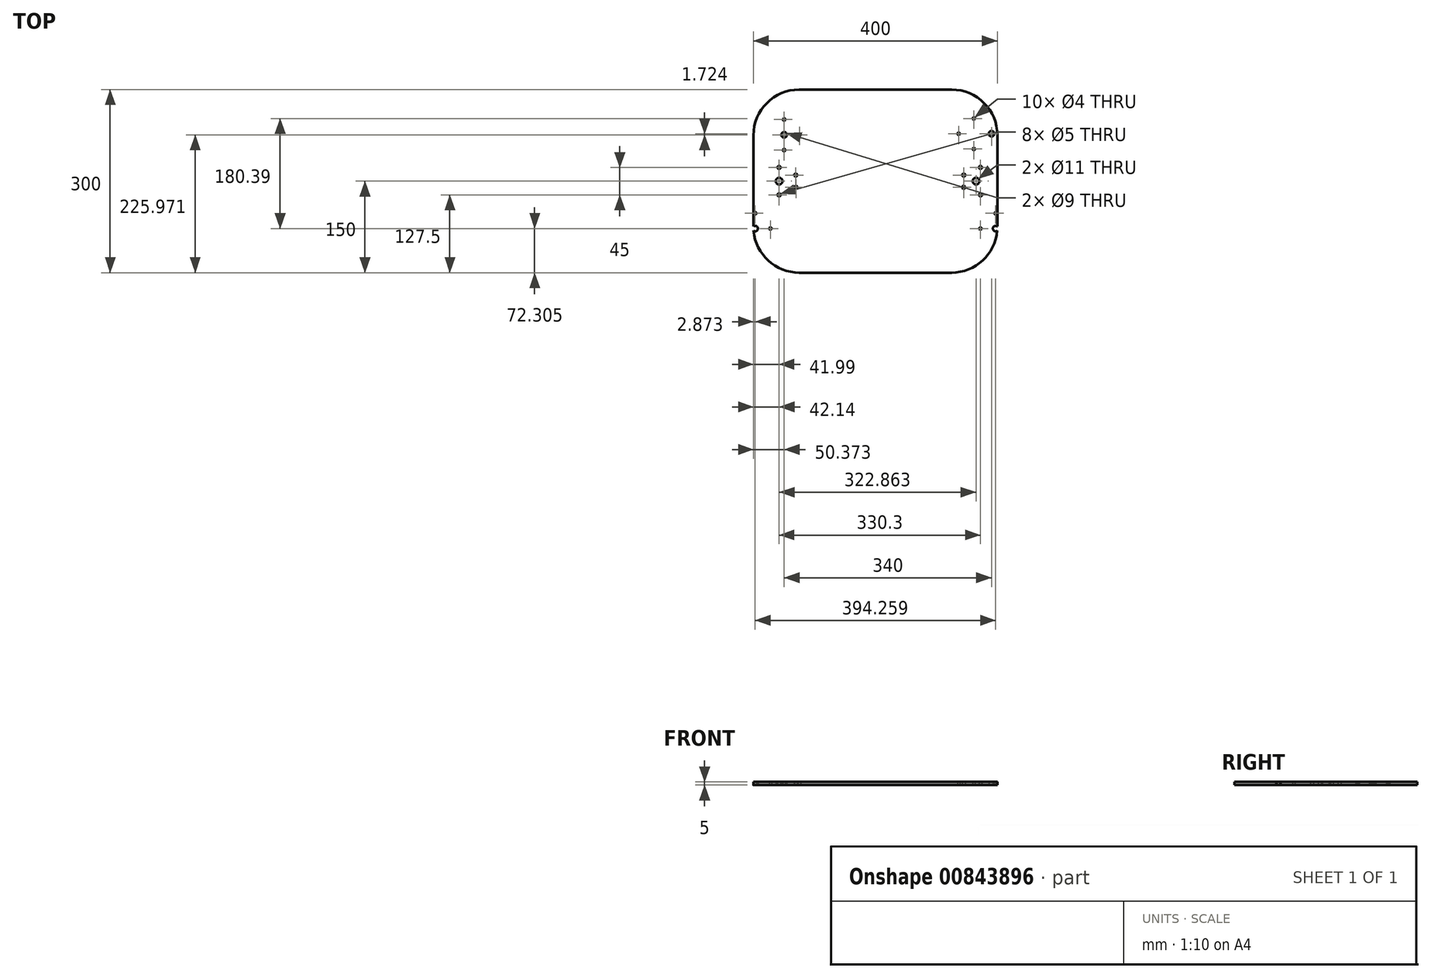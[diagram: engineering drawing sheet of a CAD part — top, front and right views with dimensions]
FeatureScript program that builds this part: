
annotation { "Feature Type Name" : "Feature", "Feature Type Description" : "" }
export const myFeature = defineFeature(function(context is Context, id is Id, definition is map)
    precondition{}
    {
        {
            var Q0;
            Q0=qCreatedBy(makeId("Top.planeOp"),FACE);
            var sketch = newSketch(context, id + "F0", { "sketchPlane" : qUnion([Q0])});
            skLineSegment(sketch, "E0.bottom", {"start": v(42.86, 0) * mm, "end": v(292.86, 0) * mm});
            skLineSegment(sketch, "E0.top", {"start": v(42.86, -300) * mm, "end": v(292.86, -300) * mm});
            skLineSegment(sketch, "E1.right", {"start": v(-32.14, -75) * mm, "end": v(-32.14, -225) * mm});
            skLineSegment(sketch, "E2.top", {"start": v(292.86, -300) * mm, "end": v(292.86, -300) * mm});
            skLineSegment(sketch, "E2.right", {"start": v(367.86, -75) * mm, "end": v(367.86, -225) * mm});
            skArc(sketch, "E3.filletArc", {"start": v(42.86, 0) * mm, "mid": v(-10.17, -21.97) * mm, "end": v(-32.14, -75) * mm});
            skArc(sketch, "E4.filletArc", {"start": v(-32.14, -225) * mm, "mid": v(-10.17, -278.03) * mm, "end": v(42.86, -300) * mm});
            skArc(sketch, "E5.filletArc", {"start": v(292.86, -300) * mm, "mid": v(345.9, -278.03) * mm, "end": v(367.86, -225) * mm});
            skPoint(sketch, "E6.visualSharp", {"position": v(367.86, 0) * mm});
            skArc(sketch, "E6.filletArc", {"start": v(367.86, -75) * mm, "mid": v(345.9, -21.97) * mm, "end": v(292.86, 0) * mm});
            skCircle(sketch, "E7", {"center": v(10, -150) * mm, "radius": 5.5 * mm});
            skCircle(sketch, "E8", {"center": v(37.5, -160) * mm, "radius": 2.5 * mm});
            skCircle(sketch, "E9", {"center": v(37.27, -140) * mm, "radius": 2.5 * mm});
            skCircle(sketch, "E10", {"center": v(9.88, -127.5) * mm, "radius": 2.5 * mm});
            skCircle(sketch, "E11", {"center": v(9.85, -172.5) * mm, "radius": 2.5 * mm});
            skLineSegment(sketch, "E12", {"start": v(167.86, 0) * mm, "end": v(167.86, -300) * mm, "construction": true});
            skLineSegment(sketch, "E13", {"start": v(367.86, -150) * mm, "end": v(-32.14, -150) * mm, "construction": true});
            skPoint(sketch, "E14", {"position": v(167.86, -150) * mm});
            skCircle(sketch, "E15.MirrorC", {"center": v(312.73, -140) * mm, "radius": 2.5 * mm});
            skCircle(sketch, "E16.MirrorC", {"center": v(340.15, -172.5) * mm, "radius": 2.5 * mm});
            skCircle(sketch, "E17.MirrorC", {"center": v(340.12, -127.5) * mm, "radius": 2.5 * mm});
            skCircle(sketch, "E18.MirrorC", {"center": v(312.5, -160) * mm, "radius": 2.5 * mm});
            skCircle(sketch, "E19.MirrorC", {"center": v(332.86, -150) * mm, "radius": 5.5 * mm});
            skSolve(sketch);
        }
        {
            var Q0;
            Q0=qCreatedBy(makeId("Top.planeOp"),FACE);
            var sketch = newSketch(context, id + "F1", { "sketchPlane" : qUnion([Q0])});
            skCircle(sketch, "E20", {"center": v(18.23, -74.03) * mm, "radius": 4.5 * mm});
            skLineSegment(sketch, "E21.0", {"start": v(53.23, -61.53) * mm, "end": v(53.23, -86.53) * mm, "construction": true});
            skLineSegment(sketch, "E21.1", {"start": v(30.73, -109.03) * mm, "end": v(5.73, -109.03) * mm, "construction": true});
            skLineSegment(sketch, "E21.3", {"start": v(5.73, -39.03) * mm, "end": v(30.73, -39.03) * mm, "construction": true});
            skLineSegment(sketch, "E22", {"start": v(30.73, -61.53) * mm, "end": v(53.23, -61.53) * mm, "construction": true});
            skLineSegment(sketch, "E23", {"start": v(30.73, -86.53) * mm, "end": v(53.23, -86.53) * mm, "construction": true});
            skLineSegment(sketch, "E24", {"start": v(5.73, -74.03) * mm, "end": v(5.73, -39.03) * mm, "construction": true});
            skLineSegment(sketch, "E25", {"start": v(30.73, -61.53) * mm, "end": v(30.73, -39.03) * mm, "construction": true});
            skLineSegment(sketch, "E26", {"start": v(5.73, -74.03) * mm, "end": v(5.73, -109.03) * mm, "construction": true});
            skLineSegment(sketch, "E27", {"start": v(30.73, -86.53) * mm, "end": v(30.73, -109.03) * mm, "construction": true});
            skCircle(sketch, "E28", {"center": v(18.23, -49.03) * mm, "radius": 2 * mm});
            skCircle(sketch, "E29", {"center": v(18.23, -99.03) * mm, "radius": 2 * mm});
            skCircle(sketch, "E30", {"center": v(43.23, -74.03) * mm, "radius": 2 * mm});
            skCircle(sketch, "E31.MirrorC", {"center": v(-29.27, -252.7) * mm, "radius": 2 * mm});
            skCircle(sketch, "E32.MirrorC", {"center": v(-4.27, -227.7) * mm, "radius": 2 * mm});
            skCircle(sketch, "E33.MirrorC", {"center": v(-29.27, -202.7) * mm, "radius": 2 * mm});
            skLineSegment(sketch, "E34.MirrorCS", {"start": v(-16.77, -240.2) * mm, "end": v(-16.77, -262.7) * mm, "construction": true});
            skCircle(sketch, "E35.MirrorC", {"center": v(-29.27, -227.7) * mm, "radius": 4.5 * mm});
            skLineSegment(sketch, "E36.MirrorCS", {"start": v(-41.77, -227.7) * mm, "end": v(-41.77, -192.7) * mm, "construction": true});
            skLineSegment(sketch, "E37.MirrorCS", {"start": v(-41.77, -262.7) * mm, "end": v(-16.77, -262.7) * mm, "construction": true});
            skLineSegment(sketch, "E38.MirrorCS", {"start": v(-41.77, -227.7) * mm, "end": v(-41.77, -262.7) * mm, "construction": true});
            skLineSegment(sketch, "E39.MirrorCS", {"start": v(-16.77, -240.2) * mm, "end": v(5.73, -240.2) * mm, "construction": true});
            skLineSegment(sketch, "E40.MirrorCS", {"start": v(-16.77, -215.2) * mm, "end": v(5.73, -215.2) * mm, "construction": true});
            skLineSegment(sketch, "E41.MirrorCS", {"start": v(-16.77, -215.2) * mm, "end": v(-16.77, -192.7) * mm, "construction": true});
            skLineSegment(sketch, "E42.MirrorCS", {"start": v(5.73, -240.2) * mm, "end": v(5.73, -215.2) * mm, "construction": true});
            skLineSegment(sketch, "E43.MirrorCS", {"start": v(-16.77, -192.7) * mm, "end": v(-41.77, -192.7) * mm, "construction": true});
            skCircle(sketch, "E44.MirrorC", {"center": v(304.27, -72.3) * mm, "radius": 2 * mm});
            skCircle(sketch, "E45.MirrorC", {"center": v(329.27, -47.3) * mm, "radius": 2 * mm});
            skLineSegment(sketch, "E46.MirrorCS", {"start": v(316.77, -107.3) * mm, "end": v(341.77, -107.3) * mm, "construction": true});
            skLineSegment(sketch, "E47.MirrorCS", {"start": v(316.77, -59.8) * mm, "end": v(294.27, -59.8) * mm, "construction": true});
            skCircle(sketch, "E48.MirrorC", {"center": v(358.23, -72.3) * mm, "radius": 4.5 * mm});
            skCircle(sketch, "E49.MirrorC", {"center": v(329.27, -97.3) * mm, "radius": 2 * mm});
            skLineSegment(sketch, "E50.MirrorCS", {"start": v(341.77, -72.3) * mm, "end": v(341.77, -37.3) * mm, "construction": true});
            skLineSegment(sketch, "E51.MirrorCS", {"start": v(294.27, -59.8) * mm, "end": v(294.27, -84.8) * mm, "construction": true});
            skLineSegment(sketch, "E52.MirrorCS", {"start": v(316.77, -59.8) * mm, "end": v(316.77, -37.3) * mm, "construction": true});
            skLineSegment(sketch, "E53.MirrorCS", {"start": v(316.77, -84.8) * mm, "end": v(316.77, -107.3) * mm, "construction": true});
            skLineSegment(sketch, "E54.MirrorCS", {"start": v(316.77, -84.8) * mm, "end": v(294.27, -84.8) * mm, "construction": true});
            skLineSegment(sketch, "E55.MirrorCS", {"start": v(341.77, -37.3) * mm, "end": v(316.77, -37.3) * mm, "construction": true});
            skLineSegment(sketch, "E56.MirrorCS", {"start": v(341.77, -72.3) * mm, "end": v(341.77, -107.3) * mm, "construction": true});
            skCircle(sketch, "E57.MirrorC", {"center": v(340, -227.7) * mm, "radius": 2 * mm});
            skCircle(sketch, "E58.MirrorC", {"center": v(365, -202.7) * mm, "radius": 2 * mm});
            skCircle(sketch, "E59.MirrorC", {"center": v(365, -252.7) * mm, "radius": 2 * mm});
            skLineSegment(sketch, "E60.MirrorCS", {"start": v(377.5, -262.7) * mm, "end": v(352.5, -262.7) * mm, "construction": true});
            skLineSegment(sketch, "E61.MirrorCS", {"start": v(330, -240.2) * mm, "end": v(330, -215.2) * mm, "construction": true});
            skLineSegment(sketch, "E62.MirrorCS", {"start": v(377.5, -227.7) * mm, "end": v(377.5, -192.7) * mm, "construction": true});
            skLineSegment(sketch, "E63.MirrorCS", {"start": v(352.5, -240.2) * mm, "end": v(352.5, -262.7) * mm, "construction": true});
            skLineSegment(sketch, "E64.MirrorCS", {"start": v(377.5, -227.7) * mm, "end": v(377.5, -262.7) * mm, "construction": true});
            skLineSegment(sketch, "E65.MirrorCS", {"start": v(352.5, -192.7) * mm, "end": v(377.5, -192.7) * mm, "construction": true});
            skCircle(sketch, "E66.MirrorC", {"center": v(365, -227.7) * mm, "radius": 4.5 * mm});
            skLineSegment(sketch, "E67.MirrorCS", {"start": v(352.5, -240.2) * mm, "end": v(330, -240.2) * mm, "construction": true});
            skLineSegment(sketch, "E68.MirrorCS", {"start": v(352.5, -215.2) * mm, "end": v(330, -215.2) * mm, "construction": true});
            skLineSegment(sketch, "E69.MirrorCS", {"start": v(352.5, -215.2) * mm, "end": v(352.5, -192.7) * mm, "construction": true});
            skPoint(sketch, "E70.startSnap0", {"position": v(18.23, -109.03) * mm});
            skSolve(sketch);
        }
        {
            var Q0;
            Q0 = qSketchRegion(id + "F0", true);
            extrude(context, id + "F2", {"entities" : qUnion([Q0]), "depth" : 5 * mm, "offsetDistance" : 25 * mm});
        }
        {
            var Q0;
            Q0 = qSketchRegion(id + "F1", true);
            extrude(context, id + "F3", {"entities" : qUnion([Q0]), "operationType" : NewBodyOperationType.REMOVE, "depth" : 25 * mm, "offsetDistance" : 25 * mm});
        }
    });
